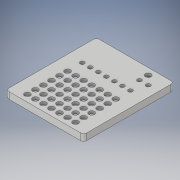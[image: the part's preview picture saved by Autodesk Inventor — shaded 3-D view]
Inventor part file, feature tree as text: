
AUTODESK INVENTOR PART (.ipt)
format: ipt  version: 2018.3 (Build 223284000, 284)  size: 313,856 bytes
history: native  units: in
note: dims shown in document units (in); Inventor stores cm internally (conversion verified against a paired STEP export)
features: extrude x5, sketch x3, fillet x1, projected_geometry x1
ambient origin geometry x8: Origin, YZ Plane, XZ Plane, XY Plane, X Axis, Y Axis, Z Axis, Center Point
bodies: Solid1 (feature_tree)
feature tree (10):
  sketch  "Sketch1"  dims[d0=2.7in d1=3.175in]
  extrude  "Extrusion1"  Depth=3.175in
  extrude  "Extrusion2"  Depth=0.1in
  extrude  "Extrusion3"  Depth=0.125in
  sketch  "Sketch3"  dims[d4=0.0591in d5=2.25in d6=2.4in d7=2.875in d9=0.15in d10=0.15in d11=0.15in d12=0.126in d13=0.1969in d14=0.1in d15=0.0in d16=0.15in d17=0.0in d18=2.3622in d20=0.3in d21=2.7559in d23=0.3in d26=0.2087in d27=2.7559in d29=0.3in d30=0.3937in d32=1.0in d34=0.3in d35=0.3in d36=2.4in d37=0.826in d38=0.1575in d40=0.39in d41=0.325in d42=0.324in d43=0.05in d44=0.0in d46=0.343in d47=0.05in d48=0.0in d49=0.304in d50=0.06in d51=0.05in d52=0.0in d53=0.1in d54=0.125in]
  extrude  "Extrusion4"  Depth=0.125in
  extrude  "Extrusion5"  Depth=0.125in
  fillet  "Fillet1"  Radius=0.15in
  sketch  "Sketch2"  dims[d2=0.1in d3=0.1in]
  projected_geometry  "Projected Loop1"
